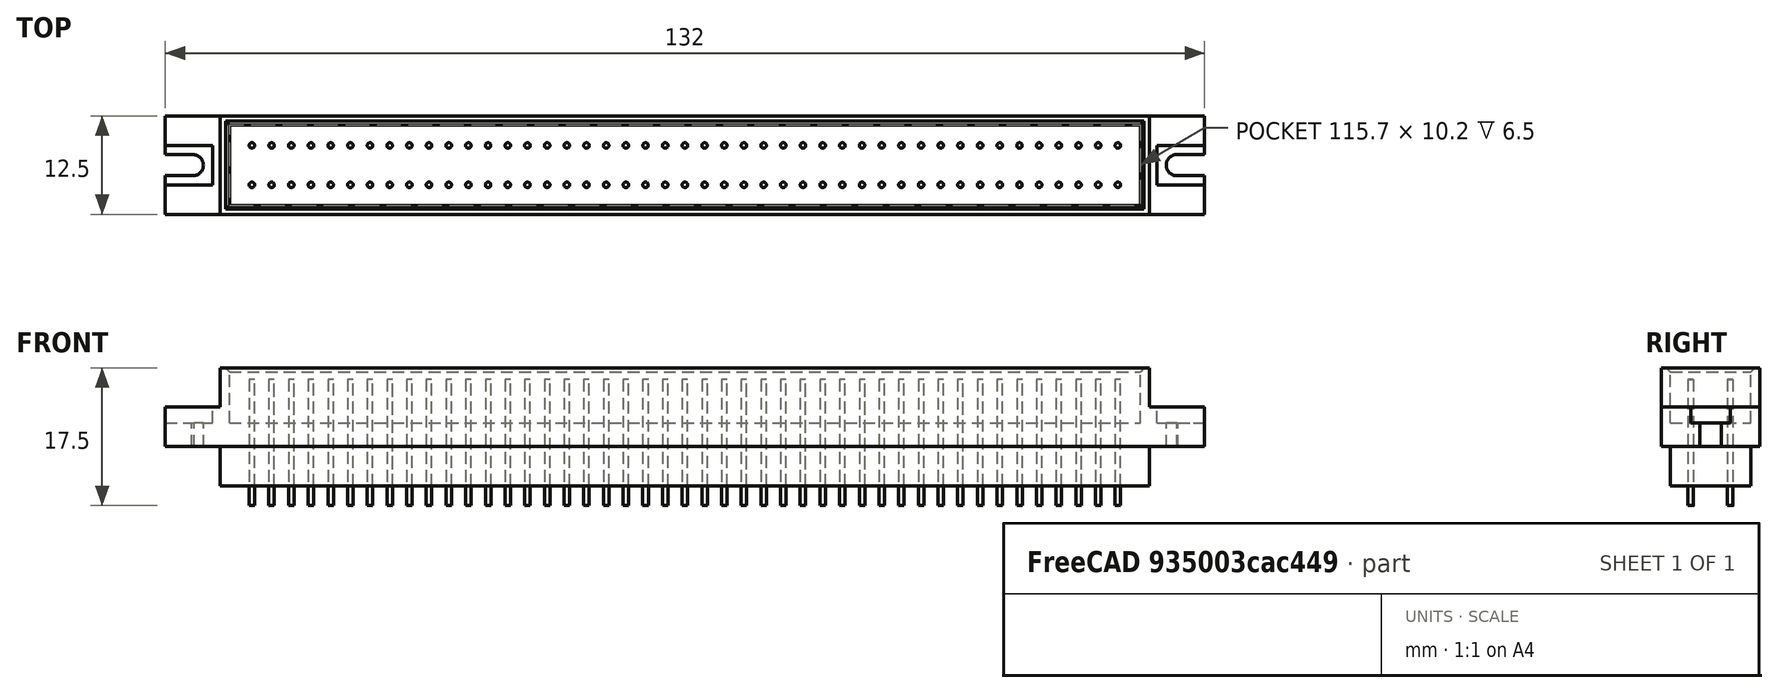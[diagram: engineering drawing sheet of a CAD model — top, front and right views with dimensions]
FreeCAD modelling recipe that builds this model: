
FCSTD DOCUMENT  (FreeCAD 0.16R6706 (Git))
Label: snp34s-90v-v
License: All rights reserved
LicenseURL: http://en.wikipedia.org/wiki/All_rights_reserved
objects: Part::Box×9, Part::Cylinder×2, Part::MultiFuse×2, Part::Cut×1, Sketcher::SketchObject×1, PartDesign::Pad×1, Part::Compound×1, Part::Chamfer×1
note: 19 computed .brp shape members not serialized (recipe doc carries the construction recipe); baked Part::Feature solids carry a one-line shape summary decoded from their .brp

FEATURE [Part::Box] Box  label="болван"
  Height = 10
  Length = 132
  Placement = pos=(-7,-1.15,5) rot=(0,0,1;0rad)
  Width = 12.5
FEATURE [Part::Box] Box001  label="пьедестал"
  Height = 5
  Length = 118
  Width = 10.2
FEATURE [Part::Box] Box002  label="-главная полость"
  Height = 7
  Length = 115.7
  Placement = pos=(1.15,0,8) rot=(0,0,1;0rad)
  Width = 10.2
FEATURE [Part::Box] Box003  label="-угол слева"
  Height = 10
  Length = 10
  Placement = pos=(-10,-2,10) rot=(0,0,1;0rad)
  Width = 14
FEATURE [Part::Box] Box004  label="-угол справа"
  Height = 10
  Length = 10
  Placement = pos=(118,-2,10) rot=(0,0,1;0rad)
  Width = 14
FEATURE [Part::Cylinder] Cylinder  label="-дырка слева"
  Angle = 360
  Height = 10
  Placement = pos=(-3.5,5.1,0) rot=(0,0,1;0rad)
  Radius = 1.35
FEATURE [Part::Cylinder] Cylinder001  label="-дырка справа"
  Angle = 360
  Height = 10
  Placement = pos=(121.5,5.1,0) rot=(0,0,1;0rad)
  Radius = 1.35
FEATURE [Part::Box] Box005  label="-фреза слева"
  Height = 10
  Length = 10
  Placement = pos=(-13.3,3.76,0) rot=(0,0,1;0rad)
  Width = 2.7
FEATURE [Part::Box] Box006  label="-фреза справа"
  Height = 10
  Length = 10
  Placement = pos=(121.5,3.76,0) rot=(0,0,1;0rad)
  Width = 2.7
FEATURE [Part::Box] Box007  label="-под гайку слева"
  Height = 10
  Length = 10
  Placement = pos=(-11,2.6,8) rot=(0,0,1;0rad)
  Width = 5
FEATURE [Part::Box] Box008  label="-под гайку справа"
  Height = 10
  Length = 10
  Placement = pos=(119,2.6,8) rot=(0,0,1;0rad)
  Width = 5
FEATURE [Part::MultiFuse] Fusion  label="минусы"
  Shapes = -> [Box002,Box004,Box006,Box003,Cylinder,Box005,Cylinder001,Box007,Box008]
FEATURE [Part::MultiFuse] Fusion001  label="плюсы"
  Shapes = -> [Box001,Box]
FEATURE [Part::Cut] Cut  label="тельце"
  Base = -> Fusion001
  Tool = -> Fusion
FEATURE [Sketcher::SketchObject] Sketch001
  sketch-geometry (117):
    g0: LineSegment [constr] StartX=1.16163 StartY=5.09496 StartZ=0 EndX=116.858 EndY=5.09496 EndZ=0
    g1: LineSegment [constr] StartX=59.0096 StartY=10.1723 StartZ=0 EndX=59.0096 EndY=0.0175944 EndZ=0
    g2: LineSegment [constr] StartX=4.00957 StartY=7.59496 StartZ=0 EndX=114.01 EndY=7.59496 EndZ=0
    g3: LineSegment [constr] StartX=114.01 StartY=7.59496 StartZ=0 EndX=114.01 EndY=2.59496 EndZ=0
    g4: LineSegment [constr] StartX=114.01 StartY=2.59496 StartZ=0 EndX=4.00957 EndY=2.59496 EndZ=0
    g5: LineSegment [constr] StartX=4.00957 StartY=2.59496 StartZ=0 EndX=4.00957 EndY=7.59496 EndZ=0
    g6: LineSegment [constr] StartX=6.50957 StartY=13.4917 StartZ=0 EndX=6.50957 EndY=-3.58481 EndZ=0
    g7: LineSegment [constr] StartX=9.00957 StartY=13.7356 StartZ=0 EndX=9.00957 EndY=-3.82876 EndZ=0
    g8: LineSegment [constr] StartX=11.5096 StartY=12.9062 StartZ=0 EndX=11.5096 EndY=-2.21869 EndZ=0
    g9: LineSegment [constr] StartX=14.0096 StartY=13.1502 StartZ=0 EndX=14.0096 EndY=-1.38926 EndZ=0
    g10: LineSegment [constr] StartX=16.5096 StartY=13.1014 StartZ=0 EndX=16.5096 EndY=-1.82837 EndZ=0
    g11: LineSegment [constr] StartX=19.0096 StartY=12.4671 StartZ=0 EndX=19.0096 EndY=-2.26748 EndZ=0
    g12: LineSegment [constr] StartX=21.5096 StartY=13.1502 StartZ=0 EndX=21.5096 EndY=-3.53602 EndZ=0
    g13: LineSegment [constr] StartX=24.0096 StartY=13.4429 StartZ=0 EndX=24.0096 EndY=-2.07232 EndZ=0
    g14: LineSegment [constr] StartX=26.5096 StartY=13.3453 StartZ=0 EndX=26.5096 EndY=-2.21869 EndZ=0
    g15: LineSegment [constr] StartX=29.0096 StartY=13.4917 StartZ=0 EndX=29.0096 EndY=-1.97474 EndZ=0
    g16: LineSegment [constr] StartX=31.5096 StartY=13.1502 StartZ=0 EndX=31.5096 EndY=-1.97474 EndZ=0
    g17: LineSegment [constr] StartX=34.0096 StartY=13.0526 StartZ=0 EndX=34.0096 EndY=-3.1457 EndZ=0
    g18: LineSegment [constr] StartX=36.5096 StartY=12.7111 StartZ=0 EndX=36.5096 EndY=-2.80417 EndZ=0
    g19: LineSegment [constr] StartX=39.0096 StartY=13.4917 StartZ=0 EndX=39.0096 EndY=-2.26748 EndZ=0
    g20: LineSegment [constr] StartX=41.5096 StartY=13.3453 StartZ=0 EndX=41.5096 EndY=-1.97474 EndZ=0
    g21: LineSegment [constr] StartX=44.0096 StartY=13.4429 StartZ=0 EndX=44.0096 EndY=-2.56022 EndZ=0
    g22: LineSegment [constr] StartX=46.5096 StartY=12.7598 StartZ=0 EndX=46.5096 EndY=-3.09691 EndZ=0
    g23: LineSegment [constr] StartX=49.0096 StartY=13.0038 StartZ=0 EndX=49.0096 EndY=-2.70659 EndZ=0
    g24: LineSegment [constr] StartX=51.5096 StartY=12.4671 StartZ=0 EndX=51.5096 EndY=-1.63321 EndZ=0
    g25: LineSegment [constr] StartX=54.0096 StartY=13.0038 StartZ=0 EndX=54.0096 EndY=-2.36506 EndZ=0
    g26: LineSegment [constr] StartX=56.5096 StartY=13.7356 StartZ=0 EndX=56.5096 EndY=-2.12111 EndZ=0
    g27: Circle CenterX=4.00957 CenterY=7.59496 CenterZ=0 NormalX=0 NormalY=0 NormalZ=1 Radius=0.35
    g28: Circle CenterX=6.50957 CenterY=7.59496 CenterZ=0 NormalX=0 NormalY=0 NormalZ=1 Radius=0.35
    g29: Circle CenterX=9.00957 CenterY=7.59496 CenterZ=0 NormalX=0 NormalY=0 NormalZ=1 Radius=0.35
    g30: Circle CenterX=11.5096 CenterY=7.59496 CenterZ=0 NormalX=0 NormalY=0 NormalZ=1 Radius=0.35
    g31: Circle CenterX=14.0096 CenterY=7.59496 CenterZ=0 NormalX=0 NormalY=0 NormalZ=1 Radius=0.35
    g32: Circle CenterX=16.5096 CenterY=7.59496 CenterZ=0 NormalX=0 NormalY=0 NormalZ=1 Radius=0.35
    g33: Circle CenterX=19.0096 CenterY=7.59496 CenterZ=0 NormalX=0 NormalY=0 NormalZ=1 Radius=0.35
    g34: Circle CenterX=21.5096 CenterY=7.59496 CenterZ=0 NormalX=0 NormalY=0 NormalZ=1 Radius=0.35
    g35: Circle CenterX=24.0096 CenterY=7.59496 CenterZ=0 NormalX=0 NormalY=0 NormalZ=1 Radius=0.35
    g36: Circle CenterX=26.5096 CenterY=7.59496 CenterZ=0 NormalX=0 NormalY=0 NormalZ=1 Radius=0.35
    g37: Circle CenterX=29.0096 CenterY=7.59496 CenterZ=0 NormalX=0 NormalY=0 NormalZ=1 Radius=0.35
    g38: Circle CenterX=31.5096 CenterY=7.59496 CenterZ=0 NormalX=0 NormalY=0 NormalZ=1 Radius=0.35
    g39: Circle CenterX=34.0096 CenterY=7.59496 CenterZ=0 NormalX=0 NormalY=0 NormalZ=1 Radius=0.35
    g40: Circle CenterX=36.5096 CenterY=7.59496 CenterZ=0 NormalX=0 NormalY=0 NormalZ=1 Radius=0.35
    g41: Circle CenterX=39.0096 CenterY=7.59496 CenterZ=0 NormalX=0 NormalY=0 NormalZ=1 Radius=0.35
    g42: Circle CenterX=41.5096 CenterY=7.59496 CenterZ=0 NormalX=0 NormalY=0 NormalZ=1 Radius=0.35
    g43: Circle CenterX=44.0096 CenterY=7.59496 CenterZ=0 NormalX=0 NormalY=0 NormalZ=1 Radius=0.35
    g44: Circle CenterX=46.5096 CenterY=7.59496 CenterZ=0 NormalX=0 NormalY=0 NormalZ=1 Radius=0.35
    g45: Circle CenterX=49.0096 CenterY=7.59496 CenterZ=0 NormalX=0 NormalY=0 NormalZ=1 Radius=0.35
    g46: Circle CenterX=51.5096 CenterY=7.59496 CenterZ=0 NormalX=0 NormalY=0 NormalZ=1 Radius=0.35
    g47: Circle CenterX=54.0096 CenterY=7.59496 CenterZ=0 NormalX=0 NormalY=0 NormalZ=1 Radius=0.35
    g48: Circle CenterX=56.5096 CenterY=7.59496 CenterZ=0 NormalX=0 NormalY=0 NormalZ=1 Radius=0.35
    g49: Circle CenterX=4.00957 CenterY=2.59496 CenterZ=0 NormalX=0 NormalY=0 NormalZ=1 Radius=0.35
    g50: Circle CenterX=6.50957 CenterY=2.59496 CenterZ=0 NormalX=0 NormalY=0 NormalZ=1 Radius=0.35
    g51: Circle CenterX=9.00957 CenterY=2.59496 CenterZ=0 NormalX=0 NormalY=0 NormalZ=1 Radius=0.35
    g52: Circle CenterX=11.5096 CenterY=2.59496 CenterZ=0 NormalX=0 NormalY=0 NormalZ=1 Radius=0.35
    g53: Circle CenterX=14.0096 CenterY=2.59496 CenterZ=0 NormalX=0 NormalY=0 NormalZ=1 Radius=0.35
    g54: Circle CenterX=16.5096 CenterY=2.59496 CenterZ=0 NormalX=0 NormalY=0 NormalZ=1 Radius=0.35
    g55: Circle CenterX=19.0096 CenterY=2.59496 CenterZ=0 NormalX=0 NormalY=0 NormalZ=1 Radius=0.35
    g56: Circle CenterX=21.5096 CenterY=2.59496 CenterZ=0 NormalX=0 NormalY=0 NormalZ=1 Radius=0.35
    g57: Circle CenterX=24.0096 CenterY=2.59496 CenterZ=0 NormalX=0 NormalY=0 NormalZ=1 Radius=0.35
    g58: Circle CenterX=26.5096 CenterY=2.59496 CenterZ=0 NormalX=0 NormalY=0 NormalZ=1 Radius=0.35
    g59: Circle CenterX=29.0096 CenterY=2.59496 CenterZ=0 NormalX=0 NormalY=0 NormalZ=1 Radius=0.35
    g60: Circle CenterX=31.5096 CenterY=2.59496 CenterZ=0 NormalX=0 NormalY=0 NormalZ=1 Radius=0.35
    g61: Circle CenterX=34.0096 CenterY=2.59496 CenterZ=0 NormalX=0 NormalY=0 NormalZ=1 Radius=0.35
    g62: Circle CenterX=36.5096 CenterY=2.59496 CenterZ=0 NormalX=0 NormalY=0 NormalZ=1 Radius=0.35
    g63: Circle CenterX=39.0096 CenterY=2.59496 CenterZ=0 NormalX=0 NormalY=0 NormalZ=1 Radius=0.35
    g64: Circle CenterX=41.5096 CenterY=2.59496 CenterZ=0 NormalX=0 NormalY=0 NormalZ=1 Radius=0.35
    g65: Circle CenterX=44.0096 CenterY=2.59496 CenterZ=0 NormalX=0 NormalY=0 NormalZ=1 Radius=0.35
    g66: Circle CenterX=46.5096 CenterY=2.59496 CenterZ=0 NormalX=0 NormalY=0 NormalZ=1 Radius=0.35
    g67: Circle CenterX=49.0096 CenterY=2.59496 CenterZ=0 NormalX=0 NormalY=0 NormalZ=1 Radius=0.35
    g68: Circle CenterX=51.5096 CenterY=2.59496 CenterZ=0 NormalX=0 NormalY=0 NormalZ=1 Radius=0.35
    g69: Circle CenterX=54.0096 CenterY=2.59496 CenterZ=0 NormalX=0 NormalY=0 NormalZ=1 Radius=0.35
    g70: Circle CenterX=56.5096 CenterY=2.59496 CenterZ=0 NormalX=0 NormalY=0 NormalZ=1 Radius=0.35
    g71: Circle CenterX=59.0096 CenterY=7.59496 CenterZ=0 NormalX=0 NormalY=0 NormalZ=1 Radius=0.35
    g72: Circle CenterX=61.5096 CenterY=7.59496 CenterZ=0 NormalX=0 NormalY=0 NormalZ=1 Radius=0.35
    g73: Circle CenterX=64.0096 CenterY=7.59496 CenterZ=0 NormalX=0 NormalY=0 NormalZ=1 Radius=0.35
    g74: Circle CenterX=66.5096 CenterY=7.59496 CenterZ=0 NormalX=0 NormalY=0 NormalZ=1 Radius=0.35
    g75: Circle CenterX=69.0096 CenterY=7.59496 CenterZ=0 NormalX=0 NormalY=0 NormalZ=1 Radius=0.35
    g76: Circle CenterX=71.5096 CenterY=7.59496 CenterZ=0 NormalX=0 NormalY=0 NormalZ=1 Radius=0.35
    g77: Circle CenterX=74.0096 CenterY=7.59496 CenterZ=0 NormalX=0 NormalY=0 NormalZ=1 Radius=0.35
    g78: Circle CenterX=76.5096 CenterY=7.59496 CenterZ=0 NormalX=0 NormalY=0 NormalZ=1 Radius=0.35
    g79: Circle CenterX=79.0096 CenterY=7.59496 CenterZ=0 NormalX=0 NormalY=0 NormalZ=1 Radius=0.35
    g80: Circle CenterX=81.5096 CenterY=7.59496 CenterZ=0 NormalX=0 NormalY=0 NormalZ=1 Radius=0.35
    g81: Circle CenterX=84.0096 CenterY=7.59496 CenterZ=0 NormalX=0 NormalY=0 NormalZ=1 Radius=0.35
    g82: Circle CenterX=86.5096 CenterY=7.59496 CenterZ=0 NormalX=0 NormalY=0 NormalZ=1 Radius=0.35
    g83: Circle CenterX=89.0096 CenterY=7.59496 CenterZ=0 NormalX=0 NormalY=0 NormalZ=1 Radius=0.35
    g84: Circle CenterX=91.5096 CenterY=7.59496 CenterZ=0 NormalX=0 NormalY=0 NormalZ=1 Radius=0.35
    g85: Circle CenterX=94.0096 CenterY=7.59496 CenterZ=0 NormalX=0 NormalY=0 NormalZ=1 Radius=0.35
    g86: Circle CenterX=96.5096 CenterY=7.59496 CenterZ=0 NormalX=0 NormalY=0 NormalZ=1 Radius=0.35
    g87: Circle CenterX=99.0096 CenterY=7.59496 CenterZ=0 NormalX=0 NormalY=0 NormalZ=1 Radius=0.35
    g88: Circle CenterX=101.51 CenterY=7.59496 CenterZ=0 NormalX=0 NormalY=0 NormalZ=1 Radius=0.35
    g89: Circle CenterX=104.01 CenterY=7.59496 CenterZ=0 NormalX=0 NormalY=0 NormalZ=1 Radius=0.35
    g90: Circle CenterX=106.51 CenterY=7.59496 CenterZ=0 NormalX=0 NormalY=0 NormalZ=1 Radius=0.35
    g91: Circle CenterX=109.01 CenterY=7.59496 CenterZ=0 NormalX=0 NormalY=0 NormalZ=1 Radius=0.35
    g92: Circle CenterX=111.51 CenterY=7.59496 CenterZ=0 NormalX=0 NormalY=0 NormalZ=1 Radius=0.35
    g93: Circle CenterX=114.01 CenterY=7.59496 CenterZ=0 NormalX=0 NormalY=0 NormalZ=1 Radius=0.35
    g94: Circle CenterX=59.0096 CenterY=2.59496 CenterZ=0 NormalX=0 NormalY=0 NormalZ=1 Radius=0.35
    g95: Circle CenterX=61.5096 CenterY=2.59496 CenterZ=0 NormalX=0 NormalY=0 NormalZ=1 Radius=0.35
    g96: Circle CenterX=64.0096 CenterY=2.59496 CenterZ=0 NormalX=0 NormalY=0 NormalZ=1 Radius=0.35
    g97: Circle CenterX=66.5096 CenterY=2.59496 CenterZ=0 NormalX=0 NormalY=0 NormalZ=1 Radius=0.35
    g98: Circle CenterX=69.0096 CenterY=2.59496 CenterZ=0 NormalX=0 NormalY=0 NormalZ=1 Radius=0.35
    g99: Circle CenterX=71.5096 CenterY=2.59496 CenterZ=0 NormalX=0 NormalY=0 NormalZ=1 Radius=0.35
    g100: Circle CenterX=74.0096 CenterY=2.59496 CenterZ=0 NormalX=0 NormalY=0 NormalZ=1 Radius=0.35
    g101: Circle CenterX=76.5096 CenterY=2.59496 CenterZ=0 NormalX=0 NormalY=0 NormalZ=1 Radius=0.35
    g102: Circle CenterX=79.0096 CenterY=2.59496 CenterZ=0 NormalX=0 NormalY=0 NormalZ=1 Radius=0.35
    g103: Circle CenterX=81.5096 CenterY=2.59496 CenterZ=0 NormalX=0 NormalY=0 NormalZ=1 Radius=0.35
    g104: Circle CenterX=84.0096 CenterY=2.59496 CenterZ=0 NormalX=0 NormalY=0 NormalZ=1 Radius=0.35
    g105: Circle CenterX=86.5096 CenterY=2.59496 CenterZ=0 NormalX=0 NormalY=0 NormalZ=1 Radius=0.35
    g106: Circle CenterX=89.0096 CenterY=2.59496 CenterZ=0 NormalX=0 NormalY=0 NormalZ=1 Radius=0.35
    g107: Circle CenterX=91.5096 CenterY=2.59496 CenterZ=0 NormalX=0 NormalY=0 NormalZ=1 Radius=0.35
    g108: Circle CenterX=94.0096 CenterY=2.59496 CenterZ=0 NormalX=0 NormalY=0 NormalZ=1 Radius=0.35
    g109: Circle CenterX=96.5096 CenterY=2.59496 CenterZ=0 NormalX=0 NormalY=0 NormalZ=1 Radius=0.35
    g110: Circle CenterX=99.0096 CenterY=2.59496 CenterZ=0 NormalX=0 NormalY=0 NormalZ=1 Radius=0.35
    g111: Circle CenterX=101.51 CenterY=2.59496 CenterZ=0 NormalX=0 NormalY=0 NormalZ=1 Radius=0.35
    g112: Circle CenterX=104.01 CenterY=2.59496 CenterZ=0 NormalX=0 NormalY=0 NormalZ=1 Radius=0.35
    g113: Circle CenterX=106.51 CenterY=2.59496 CenterZ=0 NormalX=0 NormalY=0 NormalZ=1 Radius=0.35
    g114: Circle CenterX=109.01 CenterY=2.59496 CenterZ=0 NormalX=0 NormalY=0 NormalZ=1 Radius=0.35
    g115: Circle CenterX=111.51 CenterY=2.59496 CenterZ=0 NormalX=0 NormalY=0 NormalZ=1 Radius=0.35
    g116: Circle CenterX=114.01 CenterY=2.59496 CenterZ=0 NormalX=0 NormalY=0 NormalZ=1 Radius=0.35
  constraints (233):
    c: Vertical(g1)
    c: Symmetric(g0,g0,g1)
    c: Symmetric(g1,g1,g0)
    c: Coincident(g2,g3)
    c: Coincident(g3,g4)
    c: Coincident(g4,g5)
    c: Coincident(g5,g2)
    c: Horizontal(g2)
    c: Horizontal(g4)
    c: Vertical(g3)
    c: Vertical(g5)
    c: DistanceX(g2,g2) = 110
    c: DistanceY(g3,g3) = 5
    c: Symmetric(g2,g3,g0)
    c: Symmetric(g2,g2,g1)
    c: Vertical(g6)
    c: Vertical(g7)
    c: Vertical(g8)
    c: Vertical(g9)
    c: Vertical(g10)
    c: Vertical(g11)
    c: Vertical(g12)
    c: Vertical(g13)
    c: Vertical(g14)
    c: Vertical(g15)
    c: Vertical(g16)
    c: Vertical(g17)
    c: Vertical(g18)
    c: Vertical(g19)
    c: Vertical(g20)
    c: Vertical(g21)
    c: Vertical(g22)
    c: Vertical(g23)
    c: Vertical(g24)
    c: Vertical(g25)
    c: Vertical(g26)
    c: DistanceX(g26,g1) = 2.5
    c: DistanceX(g25,g26) = 2.5
    c: DistanceX(g24,g25) = 2.5
    c: DistanceX(g23,g24) = 2.5
    c: DistanceX(g22,g23) = 2.5
    c: DistanceX(g21,g22) = 2.5
    c: DistanceX(g20,g21) = 2.5
    c: DistanceX(g19,g20) = 2.5
    c: DistanceX(g18,g19) = 2.5
    c: DistanceX(g17,g18) = 2.5
    c: DistanceX(g16,g17) = 2.5
    c: DistanceX(g15,g16) = 2.5
    c: DistanceX(g14,g15) = 2.5
    c: DistanceX(g13,g14) = 2.5
    c: DistanceX(g12,g13) = 2.5
    c: DistanceX(g11,g12) = 2.5
    c: DistanceX(g10,g11) = 2.5
    c: DistanceX(g9,g10) = 2.5
    c: DistanceX(g8,g9) = 2.5
    c: DistanceX(g7,g8) = 2.5
    c: DistanceX(g6,g7) = 2.5
    c: Equal(g27,g28)
    c: Equal(g28,g29)
    c: Equal(g29,g30)
    c: Equal(g30,g31)
    c: Equal(g31,g32)
    c: Equal(g32,g33)
    c: Equal(g33,g34)
    c: Equal(g34,g35)
    c: Equal(g35,g36)
    c: Equal(g36,g37)
    c: Equal(g37,g38)
    c: Equal(g38,g39)
    c: Equal(g39,g40)
    c: Equal(g40,g41)
    c: Equal(g41,g42)
    c: Equal(g42,g43)
    c: Equal(g43,g44)
    c: Equal(g44,g45)
    c: Equal(g45,g46)
    c: Equal(g46,g47)
    c: Equal(g47,g48)
    c: Radius(g27) = 0.35
    c: Equal(g49,g50)
    c: Equal(g50,g51)
    c: Equal(g51,g52)
    c: Equal(g52,g53)
    c: Equal(g53,g54)
    c: Equal(g54,g55)
    c: Equal(g55,g56)
    c: Equal(g56,g57)
    c: Equal(g57,g58)
    c: Equal(g58,g59)
    c: Equal(g59,g60)
    c: Equal(g60,g61)
    c: Equal(g61,g62)
    c: Equal(g62,g63)
    c: Equal(g63,g64)
    c: Equal(g64,g65)
    c: Equal(g65,g66)
    c: Equal(g66,g67)
    c: Equal(g67,g68)
    c: Equal(g68,g69)
    c: Equal(g69,g70)
    c: Equal(g27,g49) = 0.35
    c: PointOnObject(g28,g6)
    c: PointOnObject(g28,g2)
    c: PointOnObject(g29,g2)
    c: PointOnObject(g29,g7)
    c: PointOnObject(g30,g8)
    c: PointOnObject(g30,g2)
    c: PointOnObject(g31,g2)
    c: PointOnObject(g31,g9)
    c: PointOnObject(g32,g2)
    c: PointOnObject(g32,g10)
    c: PointOnObject(g33,g2)
    c: PointOnObject(g33,g11)
    c: PointOnObject(g34,g2)
    c: PointOnObject(g34,g12)
    c: PointOnObject(g35,g13)
    c: PointOnObject(g35,g2)
    c: PointOnObject(g36,g2)
    c: PointOnObject(g36,g14)
    c: PointOnObject(g37,g2)
    c: PointOnObject(g37,g15)
    c: PointOnObject(g38,g16)
    c: PointOnObject(g38,g2)
    c: PointOnObject(g39,g2)
    c: PointOnObject(g39,g17)
    c: PointOnObject(g40,g2)
    c: PointOnObject(g40,g18)
    c: PointOnObject(g41,g19)
    c: PointOnObject(g41,g2)
    c: PointOnObject(g42,g2)
    c: PointOnObject(g42,g20)
    c: PointOnObject(g43,g21)
    c: PointOnObject(g43,g2)
    c: PointOnObject(g44,g2)
    c: PointOnObject(g44,g22)
    c: PointOnObject(g45,g23)
    c: PointOnObject(g45,g2)
    c: PointOnObject(g46,g24)
    c: PointOnObject(g46,g2)
    c: PointOnObject(g47,g25)
    c: PointOnObject(g47,g2)
    c: PointOnObject(g48,g26)
    c: PointOnObject(g48,g2)
    c: PointOnObject(g70,g26)
    c: PointOnObject(g70,g4)
    c: PointOnObject(g69,g4)
    c: PointOnObject(g69,g25)
    c: PointOnObject(g68,g24)
    c: PointOnObject(g68,g4)
    c: PointOnObject(g67,g23)
    c: PointOnObject(g67,g4)
    c: PointOnObject(g66,g22)
    c: PointOnObject(g66,g4)
    c: PointOnObject(g65,g4)
    c: PointOnObject(g65,g21)
    c: PointOnObject(g64,g4)
    c: PointOnObject(g64,g20)
    c: PointOnObject(g63,g4)
    c: PointOnObject(g63,g19)
    c: PointOnObject(g62,g4)
    c: PointOnObject(g62,g18)
    c: PointOnObject(g61,g4)
    c: PointOnObject(g61,g17)
    c: PointOnObject(g60,g16)
    c: PointOnObject(g60,g4)
    c: PointOnObject(g59,g4)
    c: PointOnObject(g59,g15)
    c: PointOnObject(g58,g4)
    c: PointOnObject(g58,g14)
    c: PointOnObject(g57,g4)
    c: PointOnObject(g57,g13)
    c: PointOnObject(g56,g4)
    c: PointOnObject(g56,g12)
    c: PointOnObject(g55,g4)
    c: PointOnObject(g55,g11)
    c: PointOnObject(g54,g4)
    c: PointOnObject(g54,g10)
    c: PointOnObject(g53,g4)
    c: PointOnObject(g53,g9)
    c: PointOnObject(g52,g4)
    c: PointOnObject(g52,g8)
    c: PointOnObject(g51,g7)
    c: PointOnObject(g51,g4)
    c: PointOnObject(g50,g6)
    c: PointOnObject(g50,g4)
    c: PointOnObject(g49,g4)
    c: PointOnObject(g49,g5)
    c: Equal(g71,g72)
    c: Equal(g72,g73)
    c: Equal(g73,g74)
    c: Equal(g74,g75)
    c: Equal(g75,g76)
    c: Equal(g76,g77)
    c: Equal(g77,g78)
    c: Equal(g78,g79)
    c: Equal(g79,g80)
    c: Equal(g80,g81)
    c: Equal(g81,g82)
    c: Equal(g82,g83)
    c: Equal(g83,g84)
    c: Equal(g84,g85)
    c: Equal(g85,g86)
    c: Equal(g86,g87)
    c: Equal(g87,g88)
    c: Equal(g88,g89)
    c: Equal(g89,g90)
    c: Equal(g90,g91)
    c: Equal(g91,g92)
    c: Equal(g92,g93)
    c: Equal(g27,g71) = 0.35
    c: Equal(g94,g95)
    c: Equal(g95,g96)
    c: Equal(g96,g97)
    c: Equal(g97,g98)
    c: Equal(g98,g99)
    c: Equal(g99,g100)
    c: Equal(g100,g101)
    c: Equal(g101,g102)
    c: Equal(g102,g103)
    c: Equal(g103,g104)
    c: Equal(g104,g105)
    c: Equal(g105,g106)
    c: Equal(g106,g107)
    c: Equal(g107,g108)
    c: Equal(g108,g109)
    c: Equal(g109,g110)
    c: Equal(g110,g111)
    c: Equal(g111,g112)
    c: Equal(g112,g113)
    c: Equal(g113,g114)
    c: Equal(g114,g115)
    c: Equal(g115,g116)
    c: Equal(g71,g94) = 0.35
FEATURE [PartDesign::Pad] Pad
  Length = 16
  Length2 = 100
  Sketch = -> Sketch001
  Type = 0
FEATURE [Part::Compound] Compound
  Links = -> [Pad]
  Placement = pos=(0,0,-2.5) rot=(0,0,1;0rad)
FEATURE [Part::Chamfer] Chamfer
  Base = -> Cut
  Edges = 4 edges r=0.5: [Edge98,Edge99,Edge100,Edge101]
